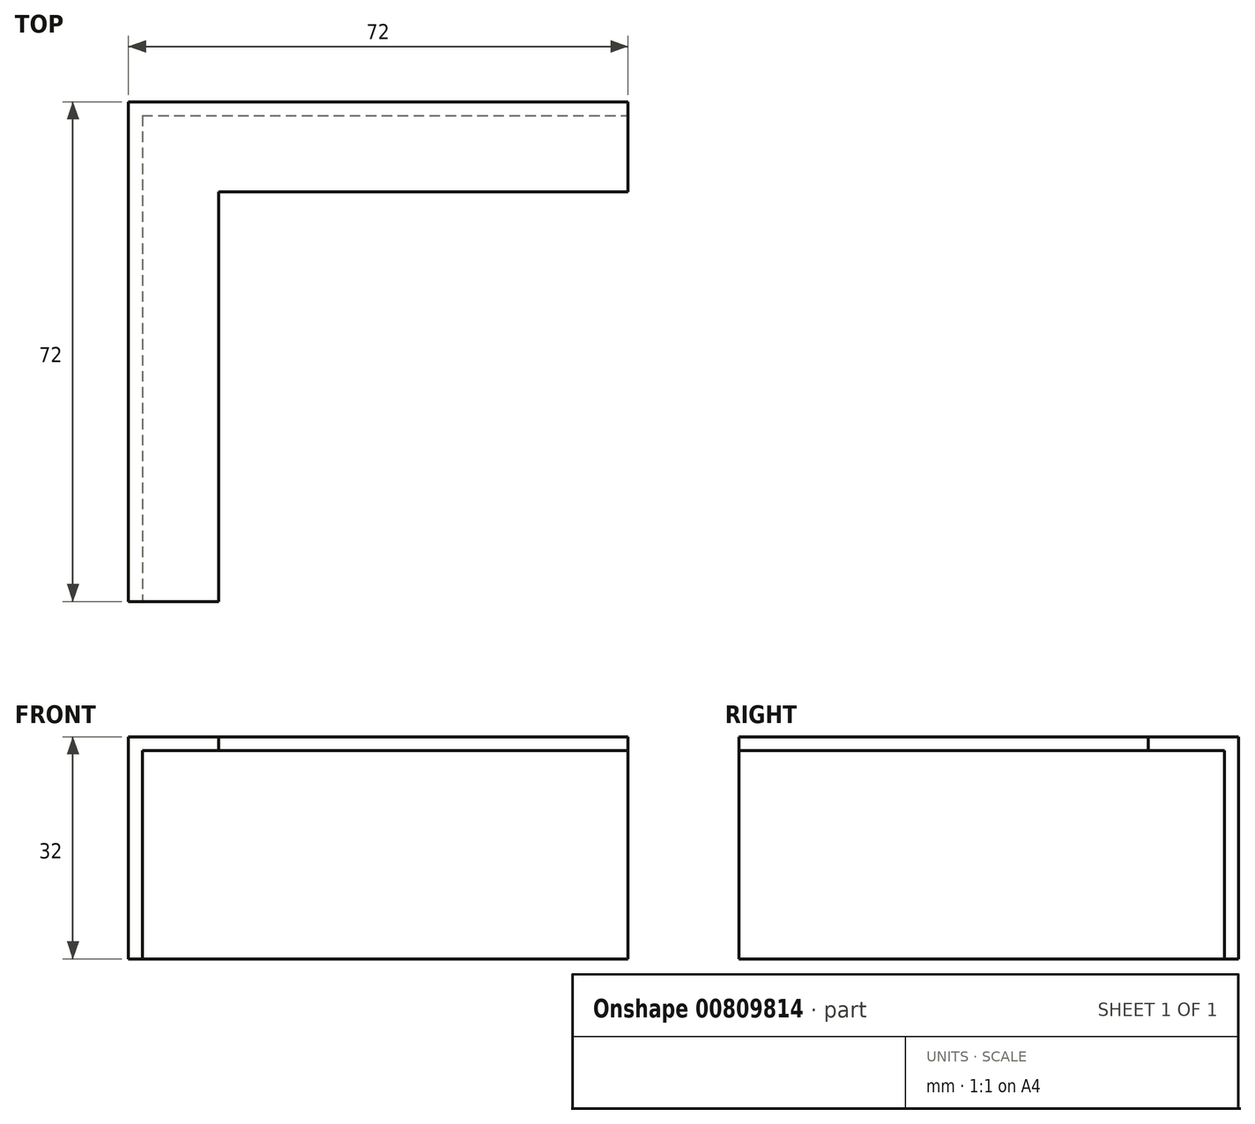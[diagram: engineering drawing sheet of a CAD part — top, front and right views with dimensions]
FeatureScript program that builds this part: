
annotation { "Feature Type Name" : "Feature", "Feature Type Description" : "" }
export const myFeature = defineFeature(function(context is Context, id is Id, definition is map)
    precondition{}
    {
        {
            var Q0;
            Q0=qCreatedBy(makeId("Top.planeOp"),FACE);
            var sketch = newSketch(context, id + "F0", { "sketchPlane" : qUnion([Q0])});
            skLineSegment(sketch, "E0.bottom", {"start": v(0, 0) * mm, "end": v(70, 0) * mm});
            skLineSegment(sketch, "E0.top", {"start": v(0, -70) * mm, "end": v(70, -70) * mm});
            skLineSegment(sketch, "E0.left", {"start": v(0, 0) * mm, "end": v(0, -70) * mm});
            skLineSegment(sketch, "E0.right", {"start": v(70, 0) * mm, "end": v(70, -70) * mm});
            skLineSegment(sketch, "E1.bottom", {"start": v(0, 0) * mm, "end": v(11, 0) * mm});
            skLineSegment(sketch, "E1.top", {"start": v(0, -11) * mm, "end": v(11, -11) * mm});
            skLineSegment(sketch, "E1.left", {"start": v(0, 0) * mm, "end": v(0, -11) * mm});
            skLineSegment(sketch, "E1.right", {"start": v(11, 0) * mm, "end": v(11, -11) * mm});
            skLineSegment(sketch, "E2.bottom", {"start": v(11, -11) * mm, "end": v(70, -11) * mm});
            skLineSegment(sketch, "E2.top", {"start": v(11, -70) * mm, "end": v(70, -70) * mm});
            skLineSegment(sketch, "E2.left", {"start": v(11, -11) * mm, "end": v(11, -70) * mm});
            skLineSegment(sketch, "E2.right", {"start": v(70, -11) * mm, "end": v(70, -70) * mm});
            skLineSegment(sketch, "E3.bottom", {"start": v(0, 0) * mm, "end": v(-2, 0) * mm});
            skLineSegment(sketch, "E3.top", {"start": v(0, 2) * mm, "end": v(-2, 2) * mm});
            skLineSegment(sketch, "E3.left", {"start": v(0, 0) * mm, "end": v(0, 2) * mm});
            skLineSegment(sketch, "E3.right", {"start": v(-2, 0) * mm, "end": v(-2, 2) * mm});
            skLineSegment(sketch, "E4.bottom", {"start": v(-2, 2) * mm, "end": v(70, 2) * mm});
            skLineSegment(sketch, "E4.top", {"start": v(-2, -70) * mm, "end": v(70, -70) * mm});
            skLineSegment(sketch, "E4.left", {"start": v(-2, 2) * mm, "end": v(-2, -70) * mm});
            skLineSegment(sketch, "E4.right", {"start": v(70, 2) * mm, "end": v(70, -70) * mm});
            skSolve(sketch);
        }
        {
            var Q0;
            {var subQ0=sQuery(id+"F0.wireOp",EDGE,"E3.bottom");Q0=makeQuery(id+"F0.imprint","IMPRINT",FACE,{"disambiguationData":[TD([[makeQuery(id+"F0.imprint","IMPRINT",EDGE,{"derivedFrom":subQ0}),-1.0]])]});}
            var Q1;
            {var subQ4=sQuery(id+"F0.wireOp",EDGE,"E0.bottom");Q1=makeQuery(id+"F0.imprint","IMPRINT",FACE,{"disambiguationData":[TD([[makeQuery(id+"F0.imprint","IMPRINT",EDGE,{"derivedFrom":subQ4}),1.0]])]});}
            var Q2;
            {var subQ0=sQuery(id+"F0.wireOp",EDGE,"E0.bottom");Q2=makeQuery(id+"F0.imprint","IMPRINT",FACE,{"disambiguationData":[TD([[makeQuery(id+"F0.imprint","IMPRINT",EDGE,{"derivedFrom":subQ0}),-1.0]])]});}
            var Q3;
            {var subQ0=sQuery(id+"F0.wireOp",EDGE,"E0.left");Q3=makeQuery(id+"F0.imprint","IMPRINT",FACE,{"disambiguationData":[TD([[makeQuery(id+"F0.imprint","IMPRINT",EDGE,{"derivedFrom":subQ0}),1.0]])]});}
            var Q4;
            {var subQ1=sQuery(id+"F0.wireOp",EDGE,"E0.left");Q4=makeQuery(id+"F0.imprint","IMPRINT",FACE,{"disambiguationData":[TD([[makeQuery(id+"F0.imprint","IMPRINT",EDGE,{"derivedFrom":subQ1}),-1.0]])]});}
            var Q5;
            Q5=makeQuery(id+"F0.imprint","IMPRINT",FACE,{"disambiguationData":[TD([[makeQuery(id+"F0.imprint","IMPRINT",EDGE,{"derivedFrom":sQuery(id+"F0.wireOp",EDGE,"E1.bottom")}),-1.0]])]});
            extrude(context, id + "F1", {"entities" : qUnion([Q0, Q1, Q2, Q3, Q4, Q5]), "depth" : 2 * mm, "offsetDistance" : 25 * mm});
        }
        {
            var Q0;
            {var subQ4=sQuery(id+"F0.wireOp",EDGE,"E0.bottom");Q0=makeQuery(id+"F0.imprint","IMPRINT",FACE,{"disambiguationData":[TD([[makeQuery(id+"F0.imprint","IMPRINT",EDGE,{"derivedFrom":subQ4}),1.0]])]});}
            var Q1;
            {var subQ1=sQuery(id+"F0.wireOp",EDGE,"E0.left");Q1=makeQuery(id+"F0.imprint","IMPRINT",FACE,{"disambiguationData":[TD([[makeQuery(id+"F0.imprint","IMPRINT",EDGE,{"derivedFrom":subQ1}),-1.0]])]});}
            var Q2;
            {var subQ0=sQuery(id+"F0.wireOp",EDGE,"E3.bottom");Q2=makeQuery(id+"F0.imprint","IMPRINT",FACE,{"disambiguationData":[TD([[makeQuery(id+"F0.imprint","IMPRINT",EDGE,{"derivedFrom":subQ0}),-1.0]])]});}
            extrude(context, id + "F2", {"entities" : qUnion([Q0, Q1, Q2]), "operationType" : NewBodyOperationType.ADD, "oppositeDirection" : true, "depth" : 30 * mm, "offsetDistance" : 25 * mm});
        }
    });
